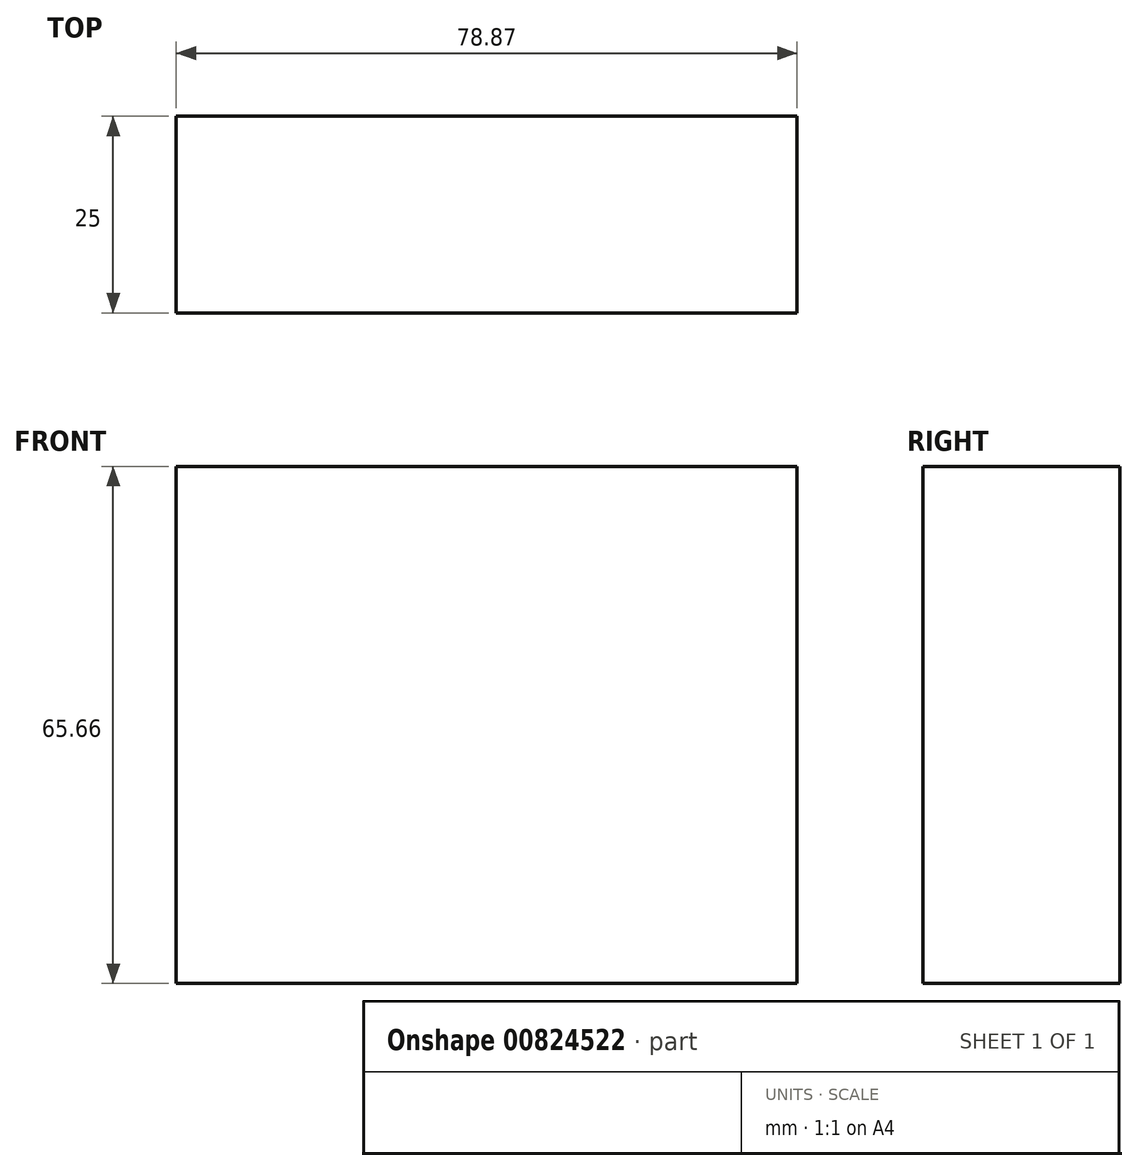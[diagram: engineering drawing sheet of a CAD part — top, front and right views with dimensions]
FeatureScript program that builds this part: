
annotation { "Feature Type Name" : "Feature", "Feature Type Description" : "" }
export const myFeature = defineFeature(function(context is Context, id is Id, definition is map)
    precondition{}
    {
        {
            var Q0;
            Q0=qCreatedBy(makeId("Front.planeOp"),FACE);
            var sketch = newSketch(context, id + "F0", { "sketchPlane" : qUnion([Q0])});
            skLineSegment(sketch, "E0.bottom", {"start": v(-90.22, 48.64) * mm, "end": v(-11.35, 48.64) * mm});
            skLineSegment(sketch, "E0.top", {"start": v(-90.22, -17.02) * mm, "end": v(-11.35, -17.02) * mm});
            skLineSegment(sketch, "E0.left", {"start": v(-90.22, 48.64) * mm, "end": v(-90.22, -17.02) * mm});
            skLineSegment(sketch, "E0.right", {"start": v(-11.35, 48.64) * mm, "end": v(-11.35, -17.02) * mm});
            skSolve(sketch);
        }
        {
            var Q0;
            Q0 = qSketchRegion(id + "F0", true);
            extrude(context, id + "F1", {"entities" : qUnion([Q0]), "depth" : 25 * mm, "offsetDistance" : 25 * mm});
        }
    });
